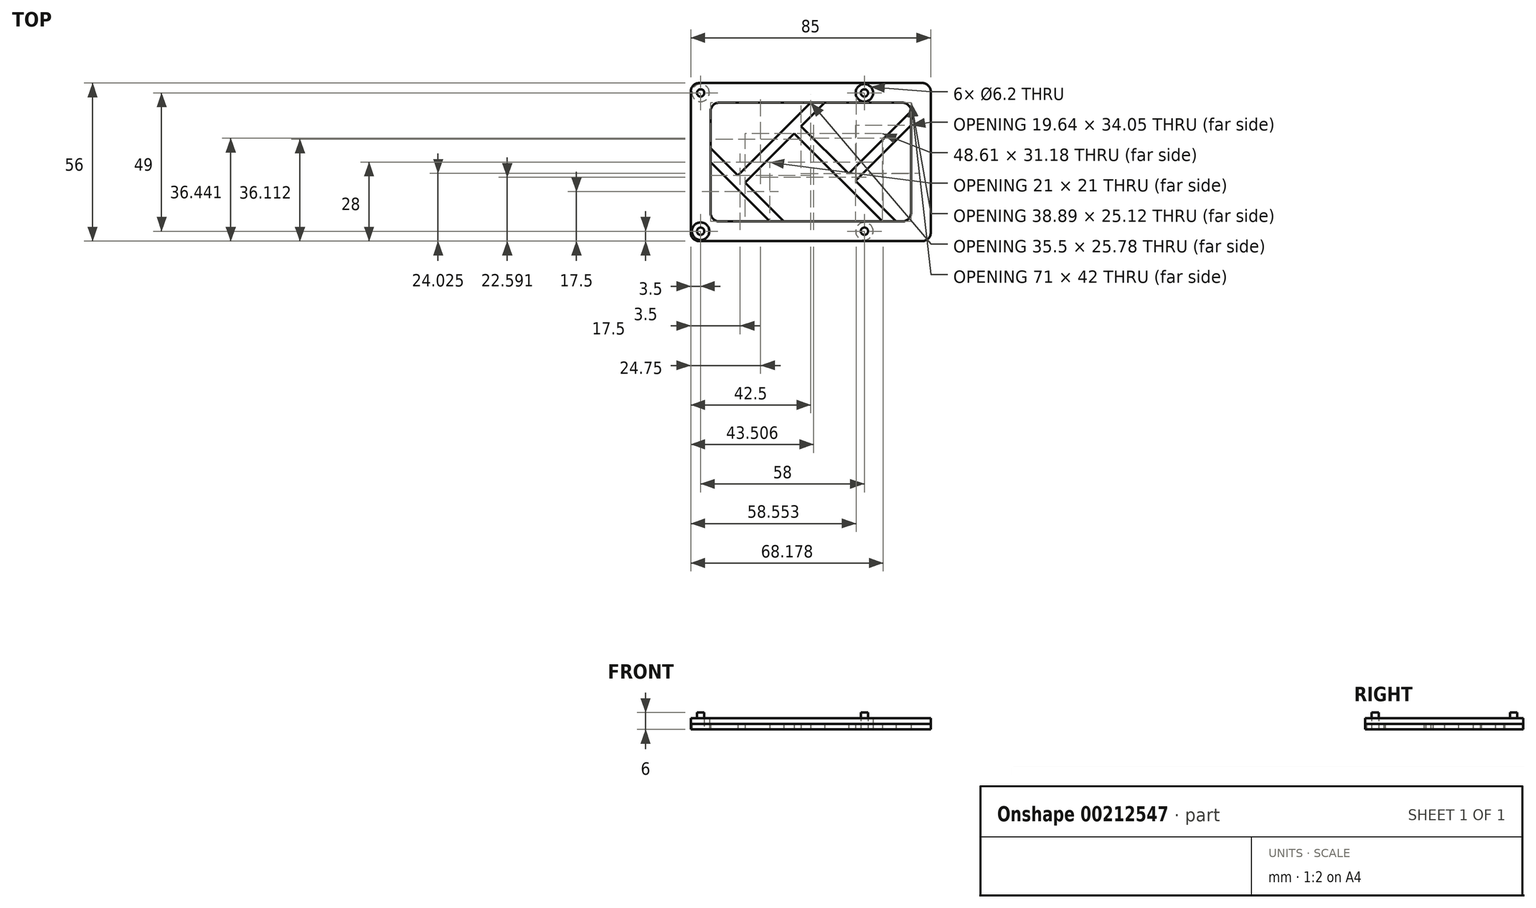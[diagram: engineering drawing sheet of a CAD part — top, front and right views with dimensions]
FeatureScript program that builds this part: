
annotation { "Feature Type Name" : "Feature", "Feature Type Description" : "" }
export const myFeature = defineFeature(function(context is Context, id is Id, definition is map)
    precondition{}
    {
        {
            var Q0;
            Q0=qCreatedBy(makeId("Top.planeOp"),FACE);
            var sketch = newSketch(context, id + "F0", { "sketchPlane" : qUnion([Q0])});
            skLineSegment(sketch, "E0.bottom", {"start": v(-39.5, 28) * mm, "end": v(39.5, 28) * mm});
            skLineSegment(sketch, "E0.top", {"start": v(-39.5, -28) * mm, "end": v(39.5, -28) * mm});
            skLineSegment(sketch, "E0.left", {"start": v(-42.5, 25) * mm, "end": v(-42.5, -25) * mm});
            skLineSegment(sketch, "E0.right", {"start": v(42.5, 25) * mm, "end": v(42.5, -25) * mm});
            skCircle(sketch, "E1", {"center": v(-39, 24.5) * mm, "radius": 3.1 * mm});
            skCircle(sketch, "E2.MirrorC", {"center": v(-39, -24.5) * mm, "radius": 3.1 * mm});
            skCircle(sketch, "E3.MirrorC", {"center": v(19, 24.5) * mm, "radius": 3.1 * mm});
            skCircle(sketch, "E4.MirrorC", {"center": v(19, -24.5) * mm, "radius": 3.1 * mm});
            skCircle(sketch, "E5", {"center": v(-39, 24.5) * mm, "radius": 1.3 * mm});
            skCircle(sketch, "E6", {"center": v(19, 24.5) * mm, "radius": 1.3 * mm});
            skCircle(sketch, "E7", {"center": v(19, -24.5) * mm, "radius": 1.3 * mm});
            skCircle(sketch, "E8", {"center": v(-39, -24.5) * mm, "radius": 1.3 * mm});
            skLineSegment(sketch, "E9.bottom", {"start": v(-32.5, 21) * mm, "end": v(32.5, 21) * mm});
            skLineSegment(sketch, "E9.top", {"start": v(-32.5, -21) * mm, "end": v(32.5, -21) * mm});
            skLineSegment(sketch, "E9.left", {"start": v(-35.5, 18) * mm, "end": v(-35.5, -18) * mm});
            skLineSegment(sketch, "E9.right", {"start": v(35.5, 18) * mm, "end": v(35.5, -18) * mm});
            skLineSegment(sketch, "E10", {"start": v(-35.5, 0) * mm, "end": v(-14.5, -21) * mm});
            skLineSegment(sketch, "E11", {"start": v(-35.5, 4.95) * mm, "end": v(-9.55, -21) * mm});
            skLineSegment(sketch, "E12", {"start": v(-25.78, -4.78) * mm, "end": v(0, 21) * mm});
            skLineSegment(sketch, "E13", {"start": v(-23.3, -7.25) * mm, "end": v(4.95, 21) * mm});
            skLineSegment(sketch, "E14", {"start": v(-5.87, 10.18) * mm, "end": v(25.31, -21) * mm});
            skLineSegment(sketch, "E15", {"start": v(-3.4, 12.66) * mm, "end": v(30.26, -21) * mm});
            skLineSegment(sketch, "E16", {"start": v(13.38, -4.12) * mm, "end": v(35.5, 18) * mm});
            skLineSegment(sketch, "E17", {"start": v(15.86, -6.6) * mm, "end": v(35.5, 13.05) * mm});
            skPoint(sketch, "E18.visualSharp", {"position": v(-42.5, 28) * mm});
            skArc(sketch, "E18.filletArc", {"start": v(-39.5, 28) * mm, "mid": v(-41.62, 27.12) * mm, "end": v(-42.5, 25) * mm});
            skPoint(sketch, "E19.visualSharp", {"position": v(42.5, 28) * mm});
            skArc(sketch, "E19.filletArc", {"start": v(42.5, 25) * mm, "mid": v(41.62, 27.12) * mm, "end": v(39.5, 28) * mm});
            skPoint(sketch, "E20.visualSharp", {"position": v(42.5, -28) * mm});
            skArc(sketch, "E20.filletArc", {"start": v(39.5, -28) * mm, "mid": v(41.62, -27.12) * mm, "end": v(42.5, -25) * mm});
            skPoint(sketch, "E21.visualSharp", {"position": v(-42.5, -28) * mm});
            skArc(sketch, "E21.filletArc", {"start": v(-42.5, -25) * mm, "mid": v(-41.62, -27.12) * mm, "end": v(-39.5, -28) * mm});
            skPoint(sketch, "E22.visualSharp", {"position": v(-35.5, -21) * mm});
            skArc(sketch, "E22.filletArc", {"start": v(-35.5, -18) * mm, "mid": v(-34.62, -20.12) * mm, "end": v(-32.5, -21) * mm});
            skPoint(sketch, "E23.visualSharp", {"position": v(-35.5, 21) * mm});
            skArc(sketch, "E23.filletArc", {"start": v(-32.5, 21) * mm, "mid": v(-34.62, 20.12) * mm, "end": v(-35.5, 18) * mm});
            skPoint(sketch, "E24.visualSharp", {"position": v(35.5, 21) * mm});
            skArc(sketch, "E24.filletArc", {"start": v(35.5, 18) * mm, "mid": v(34.62, 20.12) * mm, "end": v(32.5, 21) * mm});
            skPoint(sketch, "E25.visualSharp", {"position": v(35.5, -21) * mm});
            skArc(sketch, "E25.filletArc", {"start": v(32.5, -21) * mm, "mid": v(34.62, -20.12) * mm, "end": v(35.5, -18) * mm});
            skSolve(sketch);
        }
        {
            var Q0;
            Q0=makeQuery(id+"F0.imprint","IMPRINT",FACE,{"disambiguationData":[TD([[makeQuery(id+"F0.imprint","IMPRINT",EDGE,{"derivedFrom":sQuery(id+"F0.wireOp",EDGE,"E2.MirrorC")}),-1.0]])]});
            var Q1;
            Q1=makeQuery(id+"F0.imprint","IMPRINT",FACE,{"disambiguationData":[TD([[makeQuery(id+"F0.imprint","IMPRINT",EDGE,{"derivedFrom":sQuery(id+"F0.wireOp",EDGE,"E4.MirrorC")}),1.0]])]});
            var Q2;
            Q2=makeQuery(id+"F0.imprint","IMPRINT",FACE,{"disambiguationData":[TD([[makeQuery(id+"F0.imprint","IMPRINT",EDGE,{"derivedFrom":sQuery(id+"F0.wireOp",EDGE,"E1")}),1.0]])]});
            var Q3;
            Q3=makeQuery(id+"F0.imprint","IMPRINT",FACE,{"disambiguationData":[TD([[makeQuery(id+"F0.imprint","IMPRINT",EDGE,{"derivedFrom":sQuery(id+"F0.wireOp",EDGE,"E3.MirrorC")}),-1.0]])]});
            extrude(context, id + "F1", {"entities" : qUnion([Q0, Q1, Q2, Q3]), "depth" : 4 * mm});
        }
        {
            var Q0;
            Q0=makeQuery(id+"F0.imprint","IMPRINT",FACE,{"disambiguationData":[TD([[makeQuery(id+"F0.imprint","IMPRINT",EDGE,{"derivedFrom":sQuery(id+"F0.wireOp",EDGE,"E0.bottom")}),-1.0]])]});
            var Q1;
            {var subQ4=sQuery(id+"F0.wireOp",EDGE,"E12");Q1=makeQuery(id+"F0.imprint","IMPRINT",FACE,{"disambiguationData":[TD([[makeQuery(id+"F0.imprint","IMPRINT",EDGE,{"derivedFrom":subQ4}),-1.0]])]});}
            var Q2;
            {var subQ4=sQuery(id+"F0.wireOp",EDGE,"E10");Q2=makeQuery(id+"F0.imprint","IMPRINT",FACE,{"disambiguationData":[TD([[makeQuery(id+"F0.imprint","IMPRINT",EDGE,{"derivedFrom":subQ4}),1.0]])]});}
            var Q3;
            {var subQ4=sQuery(id+"F0.wireOp",EDGE,"E14");Q3=makeQuery(id+"F0.imprint","IMPRINT",FACE,{"disambiguationData":[TD([[makeQuery(id+"F0.imprint","IMPRINT",EDGE,{"derivedFrom":subQ4}),1.0]])]});}
            var Q4;
            {var subQ0=sQuery(id+"F0.wireOp",EDGE,"E16");Q4=makeQuery(id+"F0.imprint","IMPRINT",FACE,{"disambiguationData":[TD([[makeQuery(id+"F0.imprint","IMPRINT",EDGE,{"derivedFrom":subQ0}),-1.0]])]});}
            extrude(context, id + "F2", {"entities" : qUnion([Q0, Q1, Q2, Q3, Q4]), "depth" : 2 * mm});
        }
        {
            var Q0;
            Q0=makeQuery(id+"F0.imprint","IMPRINT",FACE,{"disambiguationData":[TD([[makeQuery(id+"F0.imprint","IMPRINT",EDGE,{"derivedFrom":sQuery(id+"F0.wireOp",EDGE,"E7")}),1.0]])]});
            var Q1;
            Q1=makeQuery(id+"F0.imprint","IMPRINT",FACE,{"disambiguationData":[TD([[makeQuery(id+"F0.imprint","IMPRINT",EDGE,{"derivedFrom":sQuery(id+"F0.wireOp",EDGE,"E8")}),1.0]])]});
            var Q2;
            Q2=makeQuery(id+"F0.imprint","IMPRINT",FACE,{"disambiguationData":[TD([[makeQuery(id+"F0.imprint","IMPRINT",EDGE,{"derivedFrom":sQuery(id+"F0.wireOp",EDGE,"E5")}),1.0]])]});
            var Q3;
            Q3=makeQuery(id+"F0.imprint","IMPRINT",FACE,{"disambiguationData":[TD([[makeQuery(id+"F0.imprint","IMPRINT",EDGE,{"derivedFrom":sQuery(id+"F0.wireOp",EDGE,"E6")}),1.0]])]});
            extrude(context, id + "F3", {"entities" : qUnion([Q0, Q1, Q2, Q3]), "operationType" : NewBodyOperationType.ADD, "depth" : 6 * mm});
        }
    });
